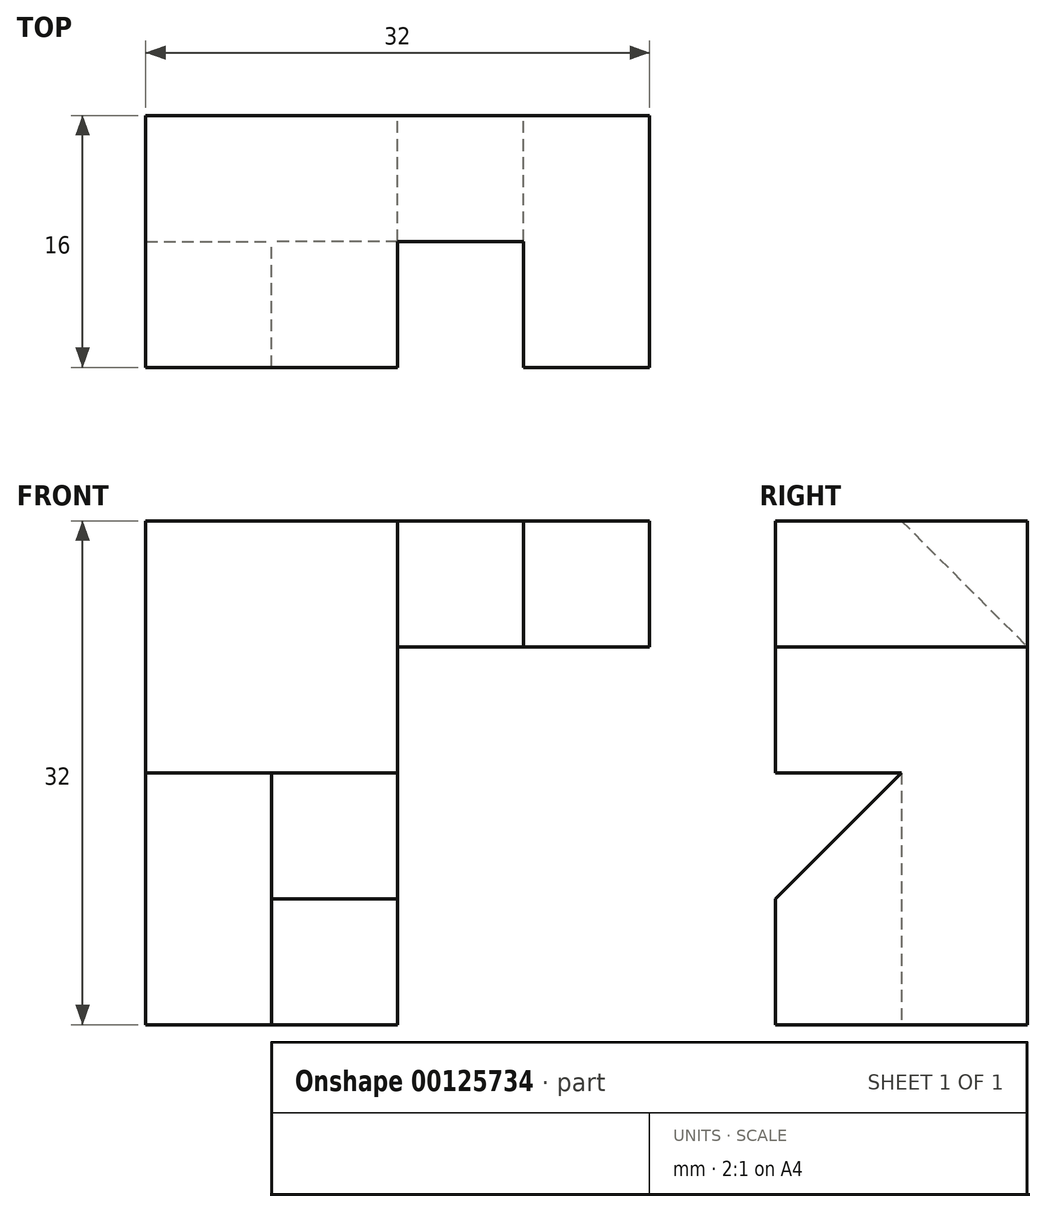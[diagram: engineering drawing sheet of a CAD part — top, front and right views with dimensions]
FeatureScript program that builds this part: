
annotation { "Feature Type Name" : "Feature", "Feature Type Description" : "" }
export const myFeature = defineFeature(function(context is Context, id is Id, definition is map)
    precondition{}
    {
        {
            var Q0;
            Q0=qCreatedBy(makeId("Front.planeOp"),FACE);
            var sketch = newSketch(context, id + "F0", { "sketchPlane" : qUnion([Q0])});
            skLineSegment(sketch, "E0.bottom", {"start": v(-60.1, 41.5) * mm, "end": v(-44.1, 41.5) * mm});
            skLineSegment(sketch, "E0.top", {"start": v(-60.1, 25.5) * mm, "end": v(-44.1, 25.5) * mm});
            skLineSegment(sketch, "E0.left", {"start": v(-60.1, 41.5) * mm, "end": v(-60.1, 25.5) * mm});
            skLineSegment(sketch, "E0.right", {"start": v(-44.1, 41.5) * mm, "end": v(-44.1, 25.5) * mm});
            skLineSegment(sketch, "E1.bottom", {"start": v(-44.1, 41.5) * mm, "end": v(-36.1, 41.5) * mm});
            skLineSegment(sketch, "E1.top", {"start": v(-44.1, 33.5) * mm, "end": v(-36.1, 33.5) * mm});
            skLineSegment(sketch, "E1.left", {"start": v(-44.1, 41.5) * mm, "end": v(-44.1, 33.5) * mm});
            skLineSegment(sketch, "E1.right", {"start": v(-36.1, 41.5) * mm, "end": v(-36.1, 33.5) * mm});
            skLineSegment(sketch, "E2.bottom", {"start": v(-36.1, 41.5) * mm, "end": v(-28.1, 41.5) * mm});
            skLineSegment(sketch, "E2.top", {"start": v(-36.1, 33.5) * mm, "end": v(-28.1, 33.5) * mm});
            skLineSegment(sketch, "E2.right", {"start": v(-28.1, 41.5) * mm, "end": v(-28.1, 33.5) * mm});
            skLineSegment(sketch, "E3.top", {"start": v(-60.1, 9.5) * mm, "end": v(-44.1, 9.5) * mm});
            skLineSegment(sketch, "E3.left", {"start": v(-60.1, 25.5) * mm, "end": v(-60.1, 9.5) * mm});
            skLineSegment(sketch, "E3.right", {"start": v(-44.1, 25.5) * mm, "end": v(-44.1, 9.5) * mm});
            skSolve(sketch);
        }
        {
            var Q0;
            Q0=makeQuery(id+"F0.imprint","IMPRINT",FACE,{"disambiguationData":[TD([[makeQuery(id+"F0.imprint","IMPRINT",EDGE,{"derivedFrom":sQuery(id+"F0.wireOp",EDGE,"E1.bottom")}),-1.0]])]});
            extrude(context, id + "F1", {"entities" : qUnion([Q0]), "depth" : 8 * mm});
        }
        {
            var Q0;
            Q0=makeQuery(id+"F0.imprint","IMPRINT",FACE,{"disambiguationData":[TD([[makeQuery(id+"F0.imprint","IMPRINT",EDGE,{"derivedFrom":sQuery(id+"F0.wireOp",EDGE,"E0.bottom")}),-1.0]])]});
            extrude(context, id + "F2", {"entities" : qUnion([Q0]), "operationType" : NewBodyOperationType.ADD, "depth" : 16 * mm});
        }
        {
            var Q0;
            Q0=makeQuery(id+"F1.opExtrude","SWEPT_FACE",FACE,{"disambiguationData":[OSD([sQuery(id+"F0.wireOp",EDGE,"E1.right")])]});
            var sketch = newSketch(context, id + "F3", { "sketchPlane" : qUnion([Q0])});
            skLineSegment(sketch, "E4", {"start": v(-8, 41.5) * mm, "end": v(0, 33.5) * mm});
            skSolve(sketch);
        }
        {
            var Q0;
            Q0=makeQuery(id+"F3.imprint","IMPRINT",FACE,{"disambiguationData":[TD([[makeQuery(id+"F3.imprint","IMPRINT",EDGE,{"derivedFrom":sQuery(id+"F3.wireOp",EDGE,"E4")}),-1.0]])]});
            extrude(context, id + "F4", {"entities" : qUnion([Q0]), "operationType" : NewBodyOperationType.REMOVE, "oppositeDirection" : true, "depth" : 8 * mm});
        }
        {
            var Q0;
            Q0=makeQuery(id+"F0.imprint","IMPRINT",FACE,{"disambiguationData":[TD([[makeQuery(id+"F0.imprint","IMPRINT",EDGE,{"derivedFrom":sQuery(id+"F0.wireOp",EDGE,"E2.bottom")}),-1.0]])]});
            extrude(context, id + "F5", {"entities" : qUnion([Q0]), "operationType" : NewBodyOperationType.ADD, "depth" : 16 * mm});
        }
        {
            var Q0;
            Q0=makeQuery(id+"F0.imprint","IMPRINT",FACE,{"disambiguationData":[TD([[makeQuery(id+"F0.imprint","IMPRINT",EDGE,{"derivedFrom":sQuery(id+"F0.wireOp",EDGE,"E0.top")}),-1.0]])]});
            extrude(context, id + "F6", {"entities" : qUnion([Q0]), "operationType" : NewBodyOperationType.ADD, "depth" : 8 * mm});
        }
        {
            var Q0;
            Q0=makeQuery(id+"F6.opExtrude","CAP_FACE",FACE,{"disambiguationData":[OSD([sQuery(id+"F0.wireOp",EDGE,"E0.top"),sQuery(id+"F0.wireOp",EDGE,"E3.top"),sQuery(id+"F0.wireOp",EDGE,"E3.left"),sQuery(id+"F0.wireOp",EDGE,"E3.right")])],"isStart":false});
            var sketch = newSketch(context, id + "F7", { "sketchPlane" : qUnion([Q0])});
            skLineSegment(sketch, "E5.bottom", {"start": v(-44.1, 25.5) * mm, "end": v(-52.1, 25.5) * mm});
            skLineSegment(sketch, "E5.top", {"start": v(-44.1, 9.5) * mm, "end": v(-52.1, 9.5) * mm});
            skLineSegment(sketch, "E5.left", {"start": v(-44.1, 25.5) * mm, "end": v(-44.1, 9.5) * mm});
            skLineSegment(sketch, "E5.right", {"start": v(-52.1, 25.5) * mm, "end": v(-52.1, 9.5) * mm});
            skSolve(sketch);
        }
        {
            var Q0;
            Q0=makeQuery(id+"F7.imprint","IMPRINT",FACE,{"disambiguationData":[TD([[makeQuery(id+"F7.imprint","IMPRINT",EDGE,{"derivedFrom":sQuery(id+"F7.wireOp",EDGE,"E5.bottom")}),-1.0]])]});
            extrude(context, id + "F8", {"entities" : qUnion([Q0]), "operationType" : NewBodyOperationType.ADD, "depth" : 8 * mm});
        }
        {
            var Q0;
            Q0=makeQuery(id+"F8.opExtrude","SWEPT_FACE",FACE,{"disambiguationData":[OSD([sQuery(id+"F7.wireOp",EDGE,"E5.right")])]});
            var sketch = newSketch(context, id + "F9", { "sketchPlane" : qUnion([Q0])});
            skLineSegment(sketch, "E6", {"start": v(16, 17.5) * mm, "end": v(8, 25.5) * mm});
            skSolve(sketch);
        }
        {
            var Q0;
            {var subQ0=sQuery(id+"F9.wireOp",EDGE,"E6");Q0=makeQuery(id+"F9.imprint","IMPRINT",FACE,{"disambiguationData":[TD([[makeQuery(id+"F9.imprint","IMPRINT",EDGE,{"derivedFrom":subQ0}),-1.0]])]});}
            extrude(context, id + "F10", {"entities" : qUnion([Q0]), "operationType" : NewBodyOperationType.REMOVE, "oppositeDirection" : true, "depth" : 8 * mm});
        }
    });
